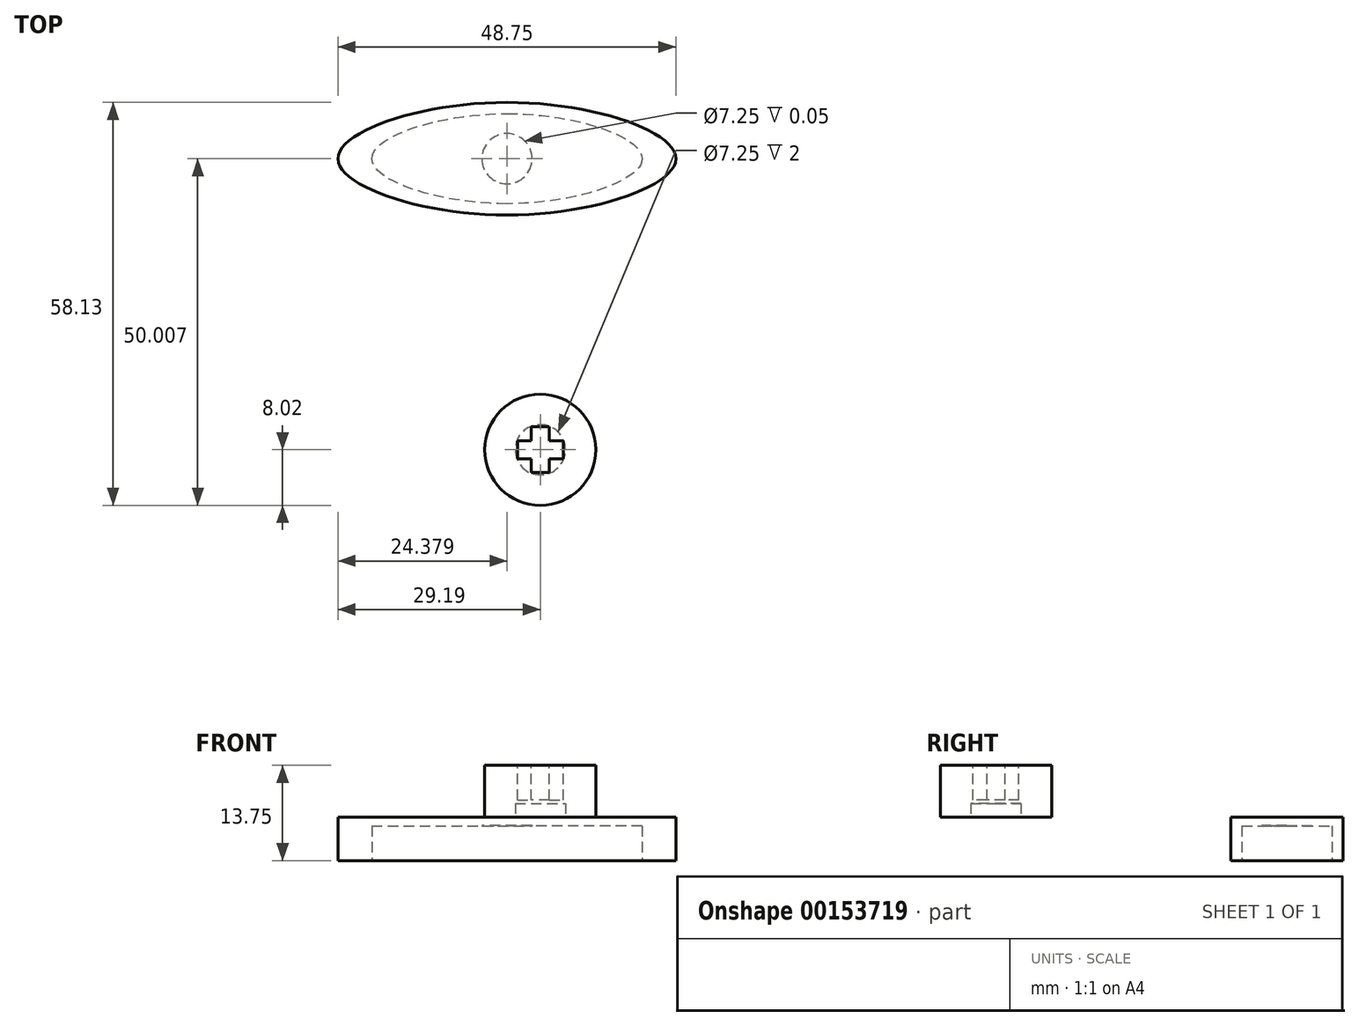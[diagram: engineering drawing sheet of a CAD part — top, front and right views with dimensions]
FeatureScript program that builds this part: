
annotation { "Feature Type Name" : "Feature", "Feature Type Description" : "" }
export const myFeature = defineFeature(function(context is Context, id is Id, definition is map)
    precondition{}
    {
        {
            var Q0;
            Q0=qCreatedBy(makeId("Top.planeOp"),FACE);
            var sketch = newSketch(context, id + "F0", { "sketchPlane" : qUnion([Q0])});
            skLineSegment(sketch, "E0", {"start": v(0, 0) * mm, "end": v(0, 6.5) * mm});
            skLineSegment(sketch, "E1", {"start": v(0, 0) * mm, "end": v(0, -6.5) * mm});
            skLineSegment(sketch, "E2", {"start": v(0, 0) * mm, "end": v(19.5, 0) * mm});
            skLineSegment(sketch, "E3", {"start": v(0, 0) * mm, "end": v(-19.5, 0) * mm});
            skFitSpline(sketch, "E4", {"points": [v(-19.5, 0) * mm, v(0, 6.5) * mm, v(19.5, 0) * mm, v(0, -6.5) * mm, v(-19.5, 0) * mm]});
            skSolve(sketch);
        }
        {
            var Q0;
            {var subQ0=sQuery(id+"F0.wireOp",EDGE,"E0");Q0=makeQuery(id+"F0.imprint","IMPRINT",FACE,{"disambiguationData":[TD([[makeQuery(id+"F0.imprint","IMPRINT",EDGE,{"derivedFrom":subQ0}),1.0]])]});}
            var Q1;
            {var subQ0=sQuery(id+"F0.wireOp",EDGE,"E0");Q1=makeQuery(id+"F0.imprint","IMPRINT",FACE,{"disambiguationData":[TD([[makeQuery(id+"F0.imprint","IMPRINT",EDGE,{"derivedFrom":subQ0}),-1.0]])]});}
            var Q2;
            {var subQ0=sQuery(id+"F0.wireOp",EDGE,"E1");Q2=makeQuery(id+"F0.imprint","IMPRINT",FACE,{"disambiguationData":[TD([[makeQuery(id+"F0.imprint","IMPRINT",EDGE,{"derivedFrom":subQ0}),1.0]])]});}
            var Q3;
            {var subQ0=sQuery(id+"F0.wireOp",EDGE,"E1");Q3=makeQuery(id+"F0.imprint","IMPRINT",FACE,{"disambiguationData":[TD([[makeQuery(id+"F0.imprint","IMPRINT",EDGE,{"derivedFrom":subQ0}),-1.0]])]});}
            extrude(context, id + "F1", {"entities" : qUnion([Q0, Q1, Q2, Q3]), "depth" : 5 * mm});
        }
        {
            var Q0;
            Q0=makeQuery(id+"F1.opExtrude","SWEPT_BODY",BODY,{"disambiguationData":[OSD([sQuery(id+"F0.wireOp",EDGE,"E4")])]});
            var Q1;
            Q1=qCreatedBy(makeId("Origin.pointOp"),VERTEX);
            transform(context, id + "F2", {"entities" : qUnion([Q0]), "transformType" : TransformType.SCALE_UNIFORMLY, "scale" : 1.25, "scalePoint" : qUnion([Q1]), "makeCopy" : true});
        }
        {
            var Q0;
            Q0=makeQuery(id+"F2.opPattern","COPY",FACE,{"derivedFrom":makeQuery(id+"F1.opExtrude","CAP_FACE",FACE,{"disambiguationData":[OSD([sQuery(id+"F0.wireOp",EDGE,"E4")])],"isStart":false}),"instanceName":"1"});
            var sketch = newSketch(context, id + "F3", { "sketchPlane" : qUnion([Q0])});
            skCircle(sketch, "E5", {"center": v(0, 0) * mm, "radius": 8.02 * mm});
            skSolve(sketch);
        }
        {
            var Q0;
            Q0=qSketchRegion(id+"F3",true);
            var Q1;
            Q1=makeQuery(id+"F3.imprint","IMPRINT",FACE,{"disambiguationData":[TD([[makeQuery(id+"F3.imprint","IMPRINT",EDGE,{"derivedFrom":sQuery(id+"F3.wireOp",EDGE,"E5")}),1.0]])]});
            extrude(context, id + "F4", {"entities" : qUnion([Q0, Q1]), "depth" : 7.5 * mm});
        }
        {
            var Q0;
            Q0=makeQuery(id+"F1.opExtrude","SWEPT_BODY",BODY,{"disambiguationData":[OSD([sQuery(id+"F0.wireOp",EDGE,"E4")])]});
            var Q1;
            Q1=makeQuery(id+"F2.opPattern","COPY",BODY,{"derivedFrom":makeQuery(id+"F1.opExtrude","SWEPT_BODY",BODY,{"disambiguationData":[OSD([sQuery(id+"F0.wireOp",EDGE,"E4")])]}),"instanceName":"1"});
            booleanBodies(context, id + "F5", {"operationType" : BooleanOperationType.SUBTRACTION, "tools" : qUnion([Q0]), "targets" : qUnion([Q1])});
        }
        {
            var Q0;
            Q0=makeQuery(id+"F4.opExtrude","CAP_FACE",FACE,{"disambiguationData":[OSD([sQuery(id+"F3.wireOp",EDGE,"E5")])],"isStart":false});
            var sketch = newSketch(context, id + "F6", { "sketchPlane" : qUnion([Q0])});
            skLineSegment(sketch, "E6.bottom", {"start": v(1.3, 3.3) * mm, "end": v(-1.3, 3.3) * mm});
            skLineSegment(sketch, "E6.top", {"start": v(1.3, -3.3) * mm, "end": v(-1.3, -3.3) * mm});
            skLineSegment(sketch, "E6.left", {"start": v(1.3, 3.3) * mm, "end": v(1.3, -3.3) * mm});
            skLineSegment(sketch, "E6.right", {"start": v(-1.3, 3.3) * mm, "end": v(-1.3, -3.3) * mm});
            skPoint(sketch, "E6.middle", {"position": v(0, 0) * mm});
            skSolve(sketch);
        }
        {
            var Q0;
            Q0=qCreatedBy(makeId("Front.planeOp"),FACE);
            var sketch = newSketch(context, id + "F7", { "sketchPlane" : qUnion([Q0])});
            skLineSegment(sketch, "E7", {"start": v(0, 0) * mm, "end": v(0, 13.86) * mm});
            skSolve(sketch);
        }
        {
            var Q0;
            Q0=makeQuery(id+"F6.imprint","IMPRINT",FACE,{"disambiguationData":[TD([[makeQuery(id+"F6.imprint","IMPRINT",EDGE,{"derivedFrom":sQuery(id+"F6.wireOp",EDGE,"E6.bottom")}),1.0]])]});
            extrude(context, id + "F8", {"entities" : qUnion([Q0]), "oppositeDirection" : true, "depth" : 5 * mm});
        }
        {
            var Q0;
            Q0=makeQuery(id+"F8.opExtrude","SWEPT_BODY",BODY,{"disambiguationData":[OSD([sQuery(id+"F6.wireOp",EDGE,"E6.bottom"),sQuery(id+"F6.wireOp",EDGE,"E6.top"),sQuery(id+"F6.wireOp",EDGE,"E6.left"),sQuery(id+"F6.wireOp",EDGE,"E6.right")])]});
            var Q1;
            Q1=qCreatedBy(makeId("Origin.pointOp"),VERTEX);
            var Q2;
            Q2=sQuery(id+"F7.wireOp",EDGE,"E7");
            transform(context, id + "F9", {"entities" : qUnion([Q0]), "transformType" : TransformType.ROTATION, "transformAxis" : qUnion([Q2]), "angle" : 90 * degree, "makeCopy" : true});
        }
        {
            var Q0;
            Q0=makeQuery(id+"F8.opExtrude","SWEPT_BODY",BODY,{"disambiguationData":[OSD([sQuery(id+"F6.wireOp",EDGE,"E6.bottom"),sQuery(id+"F6.wireOp",EDGE,"E6.top"),sQuery(id+"F6.wireOp",EDGE,"E6.left"),sQuery(id+"F6.wireOp",EDGE,"E6.right")])]});
            var Q1;
            Q1=makeQuery(id+"F9.opPattern","COPY",BODY,{"derivedFrom":makeQuery(id+"F8.opExtrude","SWEPT_BODY",BODY,{"disambiguationData":[OSD([sQuery(id+"F6.wireOp",EDGE,"E6.bottom"),sQuery(id+"F6.wireOp",EDGE,"E6.top"),sQuery(id+"F6.wireOp",EDGE,"E6.left"),sQuery(id+"F6.wireOp",EDGE,"E6.right")])]}),"instanceName":"1"});
            var Q2;
            Q2=makeQuery(id+"F4.opExtrude","SWEPT_BODY",BODY,{"disambiguationData":[OSD([sQuery(id+"F3.wireOp",EDGE,"E5")])]});
            booleanBodies(context, id + "F10", {"operationType" : BooleanOperationType.SUBTRACTION, "tools" : qUnion([Q0, Q1]), "targets" : qUnion([Q2])});
        }
        {
            var Q0;
            Q0=makeQuery(id+"F5.opBoolean","COPY",FACE,{"derivedFrom":makeQuery(id+"F1.opExtrude","CAP_FACE",FACE,{"disambiguationData":[OSD([sQuery(id+"F0.wireOp",EDGE,"E4")])],"isStart":false})});
            var sketch = newSketch(context, id + "F11", { "sketchPlane" : qUnion([Q0])});
            skCircle(sketch, "E8", {"center": v(0, 0) * mm, "radius": 3.62 * mm});
            skSolve(sketch);
        }
        {
            var Q0;
            Q0=qCreatedBy(makeId("Top.planeOp"),FACE);
            var sketch = newSketch(context, id + "F12", { "sketchPlane" : qUnion([Q0])});
            skLineSegment(sketch, "E9", {"start": v(0, 0) * mm, "end": v(-4.81, 41.99) * mm});
            skSolve(sketch);
        }
        {
            var Q0;
            Q0=makeQuery(id+"F11.imprint","IMPRINT",FACE,{"disambiguationData":[TD([[makeQuery(id+"F11.imprint","IMPRINT",EDGE,{"derivedFrom":sQuery(id+"F11.wireOp",EDGE,"E8")}),1.0]])]});
            extrude(context, id + "F13", {"entities" : qUnion([Q0]), "operationType" : NewBodyOperationType.REMOVE, "oppositeDirection" : true, "depth" : 3.25 * mm});
        }
        {
            var Q0;
            Q0=makeQuery(id+"F2.opPattern","COPY",BODY,{"derivedFrom":makeQuery(id+"F1.opExtrude","SWEPT_BODY",BODY,{"disambiguationData":[OSD([sQuery(id+"F0.wireOp",EDGE,"E4")])]}),"instanceName":"1"});
            var Q1;
            Q1=sQuery(id+"F12.wireOp",EDGE,"E9");
            transform(context, id + "F14", {"entities" : qUnion([Q0]), "transformType" : TransformType.TRANSLATION_ENTITY, "oppositeDirectionEntity" : false, "transformLine" : qUnion([Q1]), "makeCopy" : true});
        }
        {
            var Q0;
            Q0=makeQuery(id+"F14.opPattern","COPY",FACE,{"derivedFrom":makeQuery(id+"F2.opPattern","COPY",FACE,{"derivedFrom":makeQuery(id+"F1.opExtrude","CAP_FACE",FACE,{"disambiguationData":[OSD([sQuery(id+"F0.wireOp",EDGE,"E4")])],"isStart":false}),"instanceName":"1"}),"instanceName":"1"});
            var sketch = newSketch(context, id + "F15", { "sketchPlane" : qUnion([Q0])});
            skCircle(sketch, "E10", {"center": v(-4.81, 41.99) * mm, "radius": 4.3 * mm});
            skSolve(sketch);
        }
        {
            var Q0;
            Q0=makeQuery(id+"F15.imprint","IMPRINT",FACE,{"disambiguationData":[TD([[makeQuery(id+"F15.imprint","IMPRINT",EDGE,{"derivedFrom":makeQuery(id+"F14.opPattern","COPY",EDGE,{"derivedFrom":makeQuery(id+"F13.boolean.opBoolean","INTERSECT",EDGE,{"derivedFrom":[makeQuery(id+"F2.opPattern","COPY",FACE,{"derivedFrom":makeQuery(id+"F1.opExtrude","CAP_FACE",FACE,{"disambiguationData":[OSD([sQuery(id+"F0.wireOp",EDGE,"E4")])],"isStart":false}),"instanceName":"1"}),makeQuery(id+"F13.opExtrude","SWEPT_FACE",FACE,{"disambiguationData":[OSD([sQuery(id+"F11.wireOp",EDGE,"E8")])]})]}),"instanceName":"1"})}),1.0]])]});
            extrude(context, id + "F16", {"entities" : qUnion([Q0]), "operationType" : NewBodyOperationType.ADD, "oppositeDirection" : true, "depth" : 1.2 * mm});
        }
        {
            var Q0;
            Q0=makeQuery(id+"F14.opPattern","COPY",BODY,{"derivedFrom":makeQuery(id+"F2.opPattern","COPY",BODY,{"derivedFrom":makeQuery(id+"F1.opExtrude","SWEPT_BODY",BODY,{"disambiguationData":[OSD([sQuery(id+"F0.wireOp",EDGE,"E4")])]}),"instanceName":"1"}),"instanceName":"1"});
            transform(context, id + "F17", {"entities" : qUnion([Q0]), "transformType" : TransformType.TRANSLATION_3D, "dx" : 0 * mm, "dy" : 0 * mm, "dz" : 0 * mm, "makeCopy" : true});
        }
        {
            var Q0;
            Q0=makeQuery(id+"F17.opPattern","COPY",BODY,{"derivedFrom":makeQuery(id+"F14.opPattern","COPY",BODY,{"derivedFrom":makeQuery(id+"F2.opPattern","COPY",BODY,{"derivedFrom":makeQuery(id+"F1.opExtrude","SWEPT_BODY",BODY,{"disambiguationData":[OSD([sQuery(id+"F0.wireOp",EDGE,"E4")])]}),"instanceName":"1"}),"instanceName":"1"}),"instanceName":"1"});
            deleteBodies(context, id + "F18", {"entities" : qUnion([Q0])});
        }
        {
            var Q0;
            Q0=makeQuery(id+"F2.opPattern","COPY",BODY,{"derivedFrom":makeQuery(id+"F1.opExtrude","SWEPT_BODY",BODY,{"disambiguationData":[OSD([sQuery(id+"F0.wireOp",EDGE,"E4")])]}),"instanceName":"1"});
            deleteBodies(context, id + "F19", {"entities" : qUnion([Q0])});
        }
    });
